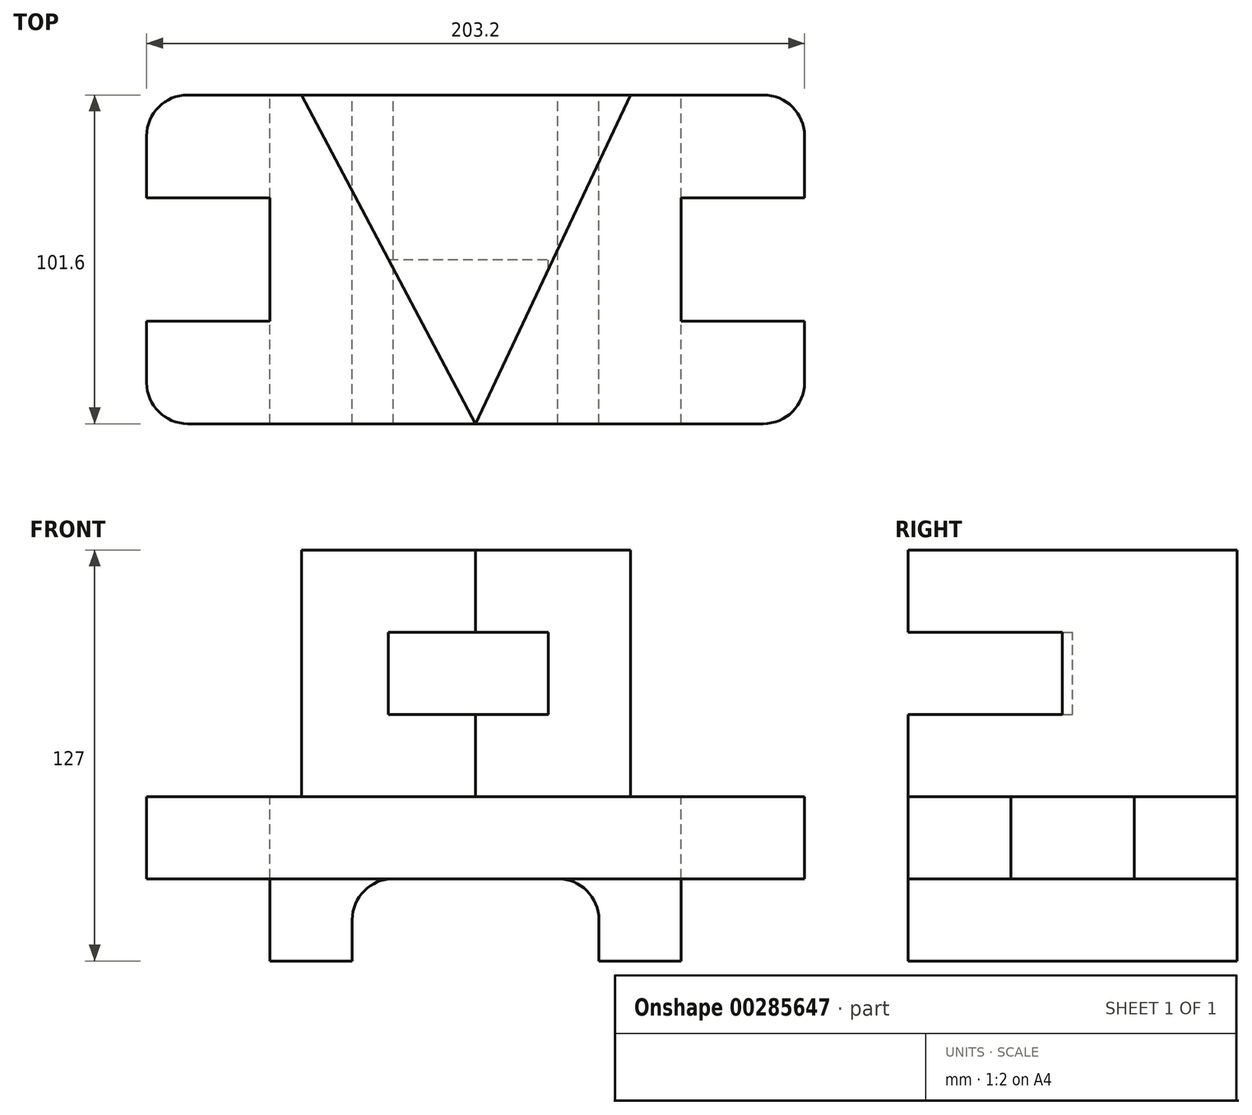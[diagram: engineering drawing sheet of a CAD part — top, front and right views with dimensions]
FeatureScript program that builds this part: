
annotation { "Feature Type Name" : "Feature", "Feature Type Description" : "" }
export const myFeature = defineFeature(function(context is Context, id is Id, definition is map)
    precondition{}
    {
        {
            var Q0;
            Q0=qCreatedBy(makeId("Front.planeOp"),FACE);
            var sketch = newSketch(context, id + "F0", { "sketchPlane" : qUnion([Q0])});
            skLineSegment(sketch, "E0", {"start": v(165.1, -25.4) * mm, "end": v(165.1, -50.8) * mm});
            skLineSegment(sketch, "E1", {"start": v(165.1, -50.8) * mm, "end": v(139.7, -50.8) * mm});
            skLineSegment(sketch, "E2", {"start": v(127, -25.4) * mm, "end": v(76.2, -25.4) * mm});
            skLineSegment(sketch, "E3", {"start": v(63.5, -50.8) * mm, "end": v(38.1, -50.8) * mm});
            skLineSegment(sketch, "E4", {"start": v(38.1, -50.8) * mm, "end": v(38.1, -25.4) * mm});
            skLineSegment(sketch, "E5", {"start": v(63.5, -50.8) * mm, "end": v(63.5, -38.1) * mm});
            skLineSegment(sketch, "E6", {"start": v(139.7, -50.8) * mm, "end": v(139.7, -38.1) * mm});
            skArc(sketch, "E7", {"start": v(76.2, -25.4) * mm, "mid": v(67.22, -29.12) * mm, "end": v(63.5, -38.1) * mm});
            skArc(sketch, "E8", {"start": v(139.7, -38.1) * mm, "mid": v(135.98, -29.12) * mm, "end": v(127, -25.4) * mm});
            skLineSegment(sketch, "E9", {"start": v(38.1, -25.4) * mm, "end": v(165.1, -25.4) * mm});
            skSolve(sketch);
        }
        {
            var Q0;
            Q0 = qSketchRegion(id + "F0", true);
            extrude(context, id + "F1", {"entities" : qUnion([Q0]), "endBound" : BoundingType.SYMMETRIC, "depth" : 101.6 * mm});
        }
        {
            var Q0;
            Q0=qCreatedBy(makeId("Front.planeOp"),FACE);
            var sketch = newSketch(context, id + "F2", { "sketchPlane" : qUnion([Q0])});
            skLineSegment(sketch, "E10", {"start": v(0, -25.4) * mm, "end": v(38.1, -25.4) * mm});
            skLineSegment(sketch, "E11", {"start": v(38.1, -25.4) * mm, "end": v(38.1, 0) * mm});
            skLineSegment(sketch, "E12", {"start": v(38.1, 0) * mm, "end": v(0, 0) * mm});
            skLineSegment(sketch, "E13", {"start": v(0, 0) * mm, "end": v(0, -25.4) * mm});
            skLineSegment(sketch, "E14.bottom", {"start": v(203.2, 0) * mm, "end": v(165.1, 0) * mm});
            skLineSegment(sketch, "E14.top", {"start": v(203.2, -25.4) * mm, "end": v(165.1, -25.4) * mm});
            skLineSegment(sketch, "E14.left", {"start": v(203.2, 0) * mm, "end": v(203.2, -25.4) * mm});
            skLineSegment(sketch, "E14.right", {"start": v(165.1, 0) * mm, "end": v(165.1, -25.4) * mm});
            skSolve(sketch);
        }
        {
            var Q0;
            Q0 = qSketchRegion(id + "F2", true);
            extrude(context, id + "F3", {"entities" : qUnion([Q0]), "operationType" : NewBodyOperationType.REMOVE, "endBound" : BoundingType.SYMMETRIC, "oppositeDirection" : true, "depth" : 38.1 * mm});
        }
        {
            var Q0;
            Q0=qCreatedBy(makeId("Top.planeOp"),FACE);
            var sketch = newSketch(context, id + "F4", { "sketchPlane" : qUnion([Q0])});
            skLineSegment(sketch, "E15", {"start": v(12.7, -50.8) * mm, "end": v(190.5, -50.8) * mm});
            skLineSegment(sketch, "E16", {"start": v(12.7, 50.8) * mm, "end": v(190.5, 50.8) * mm});
            skLineSegment(sketch, "E17", {"start": v(0, 38.1) * mm, "end": v(0, 19.05) * mm});
            skLineSegment(sketch, "E18", {"start": v(0, 19.05) * mm, "end": v(38.1, 19.05) * mm});
            skLineSegment(sketch, "E19", {"start": v(38.1, 19.05) * mm, "end": v(38.1, -19.05) * mm});
            skLineSegment(sketch, "E20", {"start": v(38.1, -19.05) * mm, "end": v(0, -19.05) * mm});
            skLineSegment(sketch, "E21", {"start": v(0, -19.05) * mm, "end": v(0, -38.1) * mm});
            skLineSegment(sketch, "E22", {"start": v(203.2, 38.1) * mm, "end": v(203.2, 19.05) * mm});
            skLineSegment(sketch, "E23", {"start": v(203.2, 19.05) * mm, "end": v(165.1, 19.05) * mm});
            skLineSegment(sketch, "E24", {"start": v(165.1, 19.05) * mm, "end": v(165.1, -19.05) * mm});
            skLineSegment(sketch, "E25", {"start": v(165.1, -19.05) * mm, "end": v(203.2, -19.05) * mm});
            skLineSegment(sketch, "E26", {"start": v(203.2, -19.05) * mm, "end": v(203.2, -38.1) * mm});
            skArc(sketch, "E27", {"start": v(12.7, 50.8) * mm, "mid": v(3.72, 47.08) * mm, "end": v(0, 38.1) * mm});
            skArc(sketch, "E28", {"start": v(203.2, 38.1) * mm, "mid": v(199.48, 47.08) * mm, "end": v(190.5, 50.8) * mm});
            skArc(sketch, "E29", {"start": v(190.5, -50.8) * mm, "mid": v(199.48, -47.08) * mm, "end": v(203.2, -38.1) * mm});
            skArc(sketch, "E30", {"start": v(0, -38.1) * mm, "mid": v(3.72, -47.08) * mm, "end": v(12.7, -50.8) * mm});
            skSolve(sketch);
        }
        {
            var Q0;
            Q0 = qSketchRegion(id + "F4", true);
            extrude(context, id + "F5", {"entities" : qUnion([Q0]), "oppositeDirection" : true, "depth" : 25.4 * mm});
        }
        {
            var Q0;
            Q0=qCreatedBy(makeId("Top.planeOp"),FACE);
            var sketch = newSketch(context, id + "F6", { "sketchPlane" : qUnion([Q0])});
            skLineSegment(sketch, "E31", {"start": v(47.82, 50.8) * mm, "end": v(149.42, 50.8) * mm});
            skLineSegment(sketch, "E32", {"start": v(149.42, 50.8) * mm, "end": v(101.6, -50.8) * mm});
            skLineSegment(sketch, "E33", {"start": v(101.6, -50.8) * mm, "end": v(47.82, 50.8) * mm});
            skSolve(sketch);
        }
        {
            var Q0;
            Q0 = qSketchRegion(id + "F6", true);
            extrude(context, id + "F7", {"entities" : qUnion([Q0]), "operationType" : NewBodyOperationType.ADD, "depth" : 76.2 * mm});
        }
        {
            var Q0;
            Q0=qCreatedBy(makeId("Front.planeOp"),FACE);
            var sketch = newSketch(context, id + "F8", { "sketchPlane" : qUnion([Q0])});
            skLineSegment(sketch, "E34", {"start": v(73.22, 50.8) * mm, "end": v(124.02, 50.8) * mm});
            skLineSegment(sketch, "E35", {"start": v(73.22, 50.8) * mm, "end": v(73.22, 25.4) * mm});
            skLineSegment(sketch, "E36", {"start": v(73.22, 25.4) * mm, "end": v(124.02, 25.4) * mm});
            skLineSegment(sketch, "E37", {"start": v(124.02, 50.8) * mm, "end": v(124.02, 25.4) * mm});
            skSolve(sketch);
        }
        {
            var Q0;
            Q0 = qSketchRegion(id + "F8", true);
            extrude(context, id + "F9", {"entities" : qUnion([Q0]), "operationType" : NewBodyOperationType.REMOVE, "endBound" : BoundingType.THROUGH_ALL, "depth" : 25.4 * mm});
        }
    });
